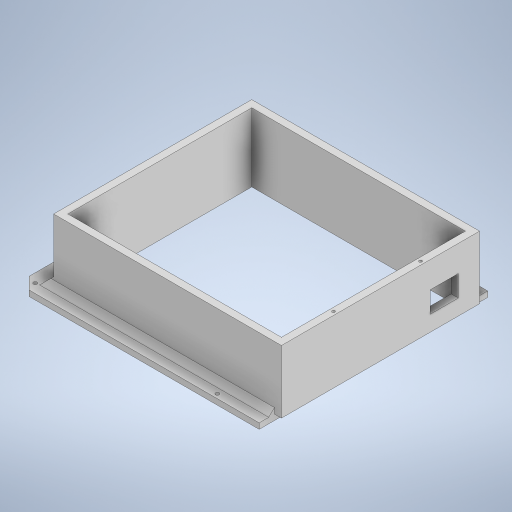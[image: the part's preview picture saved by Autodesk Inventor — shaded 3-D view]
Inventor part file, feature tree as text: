
AUTODESK INVENTOR PART (.ipt)
format: ipt  version: 2023 (Build 270158000, 158)  size: 337,920 bytes
history: native  units: in
note: dims shown in document units (in); Inventor stores cm internally (conversion verified against a paired STEP export)
features: extrude x5, sketch x5, chamfer x3, projected_geometry x1
ambient origin geometry x8: Origin, YZ Plane, XZ Plane, XY Plane, X Axis, Y Axis, Z Axis, Center Point
bodies: Solid1 (feature_tree)
feature tree (14):
  extrude  "Extrusion1"  Depth=0.1575in TaperAngle=0.0deg
  extrude  "Extrusion2"  Depth=0.0984in
  chamfer  "Chamfer1"  Distance=0.4375in
  extrude  "Extrusion3"  Depth=0.5906in
  extrude  "Extrusion4"  Depth=0.5906in TaperAngle=0.0deg
  chamfer  "Chamfer2"  Distance=0.3346in Angle=45.0deg
  chamfer  "Chamfer3"  Distance=5.9449in
  extrude  "Extrusion6"  Depth=5.1181in
  sketch  "Sketch1"  dims[d3=1.75in d4=0.0in d8=0.1575in d9=0.0in]
  sketch  "Sketch2"  dims[d10=0.0984in d11=0.0984in]
  projected_geometry  "Projected Loop1"
  sketch  "Sketch3"  dims[d12=0.0984in]
  sketch  "Sketch4"  dims[d13=0.0984in]
  sketch  "Sketch6"  dims[d14=0.0984in d18=0.4375in d19=0.0in d20=0.0787in d23=2.5625in d24=0.0in d25=0.3346in d26=0.125in d27=45.0deg d28=5.9449in d29=5.1181in d30=0.1969in d31=6.3583in d32=6.7323in d33=5.4528in d34=0.1181in d35=0.1181in d36=0.1181in d37=0.1181in d38=0.1181in d39=1.9685in d51=1.9685in d52=0.1575in d53=0.125in d54=45.0deg d55=0.2362in d56=0.125in d57=45.0deg d58=0.1181in d59=0.1181in d60=0.7874in d61=0.2756in d62=0.315in d63=1.063in d64=0.5906in d65=0.5906in d66=0.7874in d68=0.3563in d69=0.0in d70=0.5906in]
